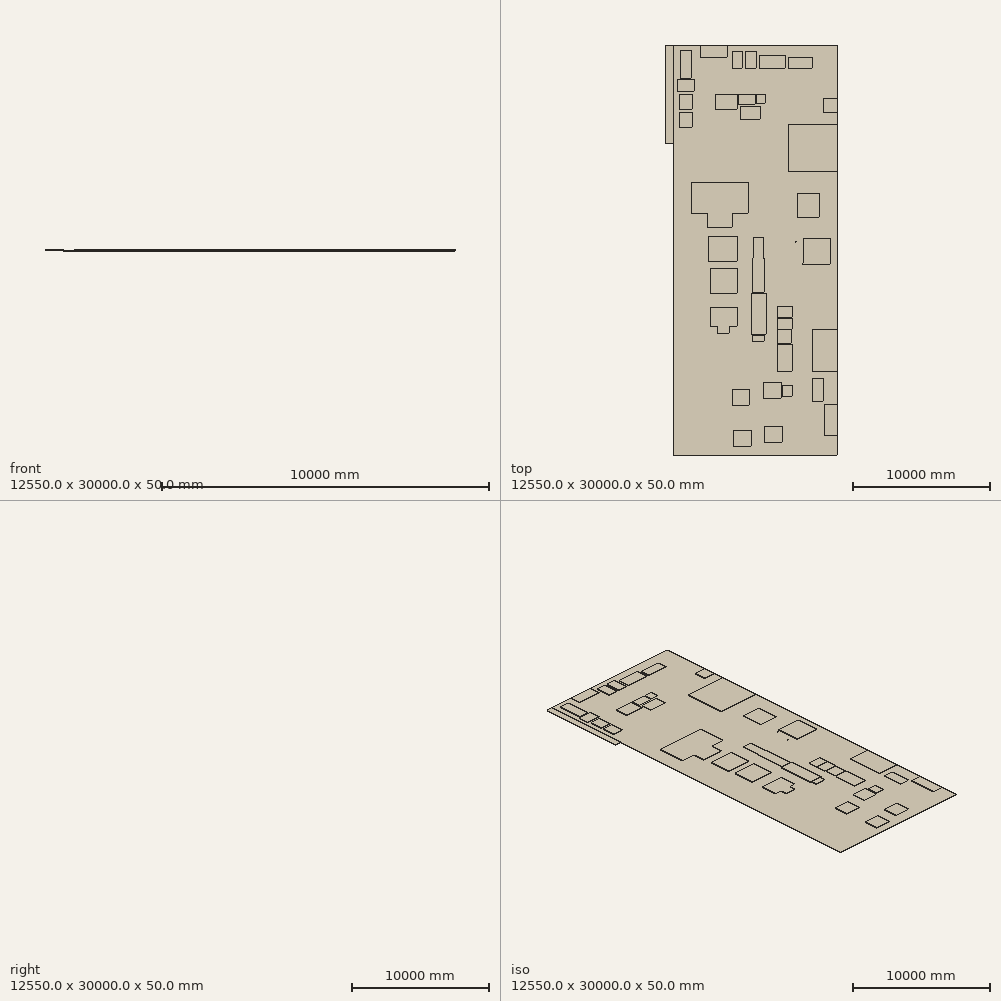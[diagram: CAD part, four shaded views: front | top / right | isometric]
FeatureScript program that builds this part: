
annotation { "Feature Type Name" : "Feature", "Feature Type Description" : "" }
export const myFeature = defineFeature(function(context is Context, id is Id, definition is map)
    precondition{}
    {
        {
            var Q0;
            Q0=qCreatedBy(makeId("Top.planeOp"),FACE);
            var sketch = newSketch(context, id + "F0", { "sketchPlane" : qUnion([Q0])});
            skLineSegment(sketch, "E0.bottom", {"start": v(6000, -15000) * mm, "end": v(-6000, -15000) * mm});
            skLineSegment(sketch, "E0.top", {"start": v(6000, 15000) * mm, "end": v(-6000, 15000) * mm});
            skLineSegment(sketch, "E0.left", {"start": v(6000, -15000) * mm, "end": v(6000, 15000) * mm});
            skLineSegment(sketch, "E0.right", {"start": v(-6000, -15000) * mm, "end": v(-6000, 15000) * mm});
            skPoint(sketch, "E0.middle", {"position": v(0, 0) * mm});
            skSolve(sketch);
        }
        {
            var Q0;
            Q0 = qSketchRegion(id + "F0", true);
            extrude(context, id + "F1", {"entities" : qUnion([Q0]), "depth" : 25 * mm, "offsetDistance" : 25 * mm});
        }
        {
            var Q0;
            Q0=makeQuery(id+"F1.opExtrude","CAP_FACE",FACE,{"disambiguationData":[OSD([sQuery(id+"F0.wireOp",EDGE,"E0.bottom"),sQuery(id+"F0.wireOp",EDGE,"E0.top"),sQuery(id+"F0.wireOp",EDGE,"E0.left"),sQuery(id+"F0.wireOp",EDGE,"E0.right")])],"isStart":false});
            var sketch = newSketch(context, id + "F2", { "sketchPlane" : qUnion([Q0])});
            skLineSegment(sketch, "E1.bottom", {"start": v(-4000, 15000) * mm, "end": v(-2000, 15000) * mm});
            skLineSegment(sketch, "E1.top", {"start": v(-4000, 14100) * mm, "end": v(-2000, 14100) * mm});
            skLineSegment(sketch, "E1.left", {"start": v(-4000, 15000) * mm, "end": v(-4000, 14100) * mm});
            skLineSegment(sketch, "E1.right", {"start": v(-2000, 15000) * mm, "end": v(-2000, 14100) * mm});
            skLineSegment(sketch, "E2.bottom", {"start": v(-1700, 14550) * mm, "end": v(-900, 14550) * mm});
            skLineSegment(sketch, "E2.top", {"start": v(-1700, 13300) * mm, "end": v(-900, 13300) * mm});
            skLineSegment(sketch, "E2.left", {"start": v(-1700, 14550) * mm, "end": v(-1700, 13300) * mm});
            skLineSegment(sketch, "E2.right", {"start": v(-900, 14550) * mm, "end": v(-900, 13300) * mm});
            skLineSegment(sketch, "E3.bottom", {"start": v(-700, 14550) * mm, "end": v(100, 14550) * mm});
            skLineSegment(sketch, "E3.top", {"start": v(-700, 13300) * mm, "end": v(100, 13300) * mm});
            skLineSegment(sketch, "E3.left", {"start": v(-700, 14550) * mm, "end": v(-700, 13300) * mm});
            skLineSegment(sketch, "E3.right", {"start": v(100, 14550) * mm, "end": v(100, 13300) * mm});
            skSolve(sketch);
        }
        {
            var Q0;
            Q0 = qSketchRegion(id + "F2", true);
            extrude(context, id + "F3", {"entities" : qUnion([Q0]), "depth" : 25 * mm, "offsetDistance" : 25 * mm});
        }
        {
            var Q0;
            Q0=makeQuery(id+"F1.opExtrude","CAP_FACE",FACE,{"disambiguationData":[OSD([sQuery(id+"F0.wireOp",EDGE,"E0.bottom"),sQuery(id+"F0.wireOp",EDGE,"E0.top"),sQuery(id+"F0.wireOp",EDGE,"E0.left"),sQuery(id+"F0.wireOp",EDGE,"E0.right")])],"isStart":false});
            var sketch = newSketch(context, id + "F4", { "sketchPlane" : qUnion([Q0])});
            skLineSegment(sketch, "E4.bottom", {"start": v(300, 14300) * mm, "end": v(2200, 14300) * mm});
            skLineSegment(sketch, "E4.top", {"start": v(300, 13300) * mm, "end": v(2200, 13300) * mm});
            skLineSegment(sketch, "E4.left", {"start": v(300, 14300) * mm, "end": v(300, 13300) * mm});
            skLineSegment(sketch, "E4.right", {"start": v(2200, 14300) * mm, "end": v(2200, 13300) * mm});
            skLineSegment(sketch, "E5.bottom", {"start": v(2400, 13300) * mm, "end": v(4200, 13300) * mm});
            skLineSegment(sketch, "E5.top", {"start": v(2400, 14100) * mm, "end": v(4200, 14100) * mm});
            skLineSegment(sketch, "E5.left", {"start": v(2400, 13300) * mm, "end": v(2400, 14100) * mm});
            skLineSegment(sketch, "E5.right", {"start": v(4200, 13300) * mm, "end": v(4200, 14100) * mm});
            skSolve(sketch);
        }
        {
            var Q0;
            Q0 = qSketchRegion(id + "F4", true);
            extrude(context, id + "F5", {"entities" : qUnion([Q0]), "depth" : 25 * mm, "offsetDistance" : 25 * mm});
        }
        {
            var Q0;
            Q0=makeQuery(id+"F1.opExtrude","CAP_FACE",FACE,{"disambiguationData":[OSD([sQuery(id+"F0.wireOp",EDGE,"E0.bottom"),sQuery(id+"F0.wireOp",EDGE,"E0.top"),sQuery(id+"F0.wireOp",EDGE,"E0.left"),sQuery(id+"F0.wireOp",EDGE,"E0.right")])],"isStart":false});
            var sketch = newSketch(context, id + "F6", { "sketchPlane" : qUnion([Q0])});
            skLineSegment(sketch, "E6.bottom", {"start": v(6000, 11100) * mm, "end": v(5000, 11100) * mm});
            skLineSegment(sketch, "E6.top", {"start": v(6000, 10100) * mm, "end": v(5000, 10100) * mm});
            skLineSegment(sketch, "E6.left", {"start": v(6000, 11100) * mm, "end": v(6000, 10100) * mm});
            skLineSegment(sketch, "E6.right", {"start": v(5000, 11100) * mm, "end": v(5000, 10100) * mm});
            skSolve(sketch);
        }
        {
            var Q0;
            Q0 = qSketchRegion(id + "F6", true);
            extrude(context, id + "F7", {"entities" : qUnion([Q0]), "depth" : 25 * mm, "offsetDistance" : 25 * mm});
        }
        {
            var Q0;
            Q0=makeQuery(id+"F1.opExtrude","CAP_FACE",FACE,{"disambiguationData":[OSD([sQuery(id+"F0.wireOp",EDGE,"E0.bottom"),sQuery(id+"F0.wireOp",EDGE,"E0.top"),sQuery(id+"F0.wireOp",EDGE,"E0.left"),sQuery(id+"F0.wireOp",EDGE,"E0.right")])],"isStart":false});
            var sketch = newSketch(context, id + "F8", { "sketchPlane" : qUnion([Q0])});
            skLineSegment(sketch, "E7.bottom", {"start": v(-2900, 11400) * mm, "end": v(-1300, 11400) * mm});
            skLineSegment(sketch, "E7.top", {"start": v(-2900, 10300) * mm, "end": v(-1300, 10300) * mm});
            skLineSegment(sketch, "E7.left", {"start": v(-2900, 11400) * mm, "end": v(-2900, 10300) * mm});
            skLineSegment(sketch, "E7.right", {"start": v(-1300, 11400) * mm, "end": v(-1300, 10300) * mm});
            skLineSegment(sketch, "E8.bottom", {"start": v(-1200, 11400) * mm, "end": v(0, 11400) * mm});
            skLineSegment(sketch, "E8.top", {"start": v(-1200, 10700) * mm, "end": v(0, 10700) * mm});
            skLineSegment(sketch, "E8.left", {"start": v(-1200, 11400) * mm, "end": v(-1200, 10700) * mm});
            skLineSegment(sketch, "E8.right", {"start": v(0, 11400) * mm, "end": v(0, 10700) * mm});
            skLineSegment(sketch, "E9.bottom", {"start": v(100, 11400) * mm, "end": v(750, 11400) * mm});
            skLineSegment(sketch, "E9.top", {"start": v(100, 10750) * mm, "end": v(750, 10750) * mm});
            skLineSegment(sketch, "E9.left", {"start": v(100, 11400) * mm, "end": v(100, 10750) * mm});
            skLineSegment(sketch, "E9.right", {"start": v(750, 11400) * mm, "end": v(750, 10750) * mm});
            skSolve(sketch);
        }
        {
            var Q0;
            Q0 = qSketchRegion(id + "F8", true);
            extrude(context, id + "F9", {"entities" : qUnion([Q0]), "depth" : 25 * mm, "offsetDistance" : 25 * mm});
        }
        {
            var Q0;
            Q0=makeQuery(id+"F1.opExtrude","CAP_FACE",FACE,{"disambiguationData":[OSD([sQuery(id+"F0.wireOp",EDGE,"E0.bottom"),sQuery(id+"F0.wireOp",EDGE,"E0.top"),sQuery(id+"F0.wireOp",EDGE,"E0.left"),sQuery(id+"F0.wireOp",EDGE,"E0.right")])],"isStart":false});
            var sketch = newSketch(context, id + "F10", { "sketchPlane" : qUnion([Q0])});
            skLineSegment(sketch, "E10.bottom", {"start": v(-1100, 10500) * mm, "end": v(400, 10500) * mm});
            skLineSegment(sketch, "E10.top", {"start": v(-1100, 9600) * mm, "end": v(400, 9600) * mm});
            skLineSegment(sketch, "E10.left", {"start": v(-1100, 10500) * mm, "end": v(-1100, 9600) * mm});
            skLineSegment(sketch, "E10.right", {"start": v(400, 10500) * mm, "end": v(400, 9600) * mm});
            skSolve(sketch);
        }
        {
            var Q0;
            Q0 = qSketchRegion(id + "F10", true);
            extrude(context, id + "F11", {"entities" : qUnion([Q0]), "depth" : 25 * mm, "offsetDistance" : 25 * mm});
        }
        {
            var Q0;
            Q0=makeQuery(id+"F1.opExtrude","CAP_FACE",FACE,{"disambiguationData":[OSD([sQuery(id+"F0.wireOp",EDGE,"E0.bottom"),sQuery(id+"F0.wireOp",EDGE,"E0.top"),sQuery(id+"F0.wireOp",EDGE,"E0.left"),sQuery(id+"F0.wireOp",EDGE,"E0.right")])],"isStart":false});
            var sketch = newSketch(context, id + "F12", { "sketchPlane" : qUnion([Q0])});
            skLineSegment(sketch, "E11.bottom", {"start": v(-5500, 14600) * mm, "end": v(-4650, 14600) * mm});
            skLineSegment(sketch, "E11.top", {"start": v(-5500, 12600) * mm, "end": v(-4650, 12600) * mm});
            skLineSegment(sketch, "E11.left", {"start": v(-5500, 14600) * mm, "end": v(-5500, 12600) * mm});
            skLineSegment(sketch, "E11.right", {"start": v(-4650, 14600) * mm, "end": v(-4650, 12600) * mm});
            skLineSegment(sketch, "E12.bottom", {"start": v(-5675, 12500) * mm, "end": v(-4475, 12500) * mm});
            skLineSegment(sketch, "E12.top", {"start": v(-5675, 11600) * mm, "end": v(-4475, 11600) * mm});
            skLineSegment(sketch, "E12.left", {"start": v(-5675, 12500) * mm, "end": v(-5675, 11600) * mm});
            skLineSegment(sketch, "E12.right", {"start": v(-4475, 12500) * mm, "end": v(-4475, 11600) * mm});
            skLineSegment(sketch, "E13.bottom", {"start": v(-5525, 11400) * mm, "end": v(-4625, 11400) * mm});
            skLineSegment(sketch, "E13.top", {"start": v(-5525, 10300) * mm, "end": v(-4625, 10300) * mm});
            skLineSegment(sketch, "E13.left", {"start": v(-5525, 11400) * mm, "end": v(-5525, 10300) * mm});
            skLineSegment(sketch, "E13.right", {"start": v(-4625, 11400) * mm, "end": v(-4625, 10300) * mm});
            skLineSegment(sketch, "E14.bottom", {"start": v(-5525, 10100) * mm, "end": v(-4625, 10100) * mm});
            skLineSegment(sketch, "E14.top", {"start": v(-5525, 9000) * mm, "end": v(-4625, 9000) * mm});
            skLineSegment(sketch, "E14.left", {"start": v(-5525, 10100) * mm, "end": v(-5525, 9000) * mm});
            skLineSegment(sketch, "E14.right", {"start": v(-4625, 10100) * mm, "end": v(-4625, 9000) * mm});
            skSolve(sketch);
        }
        {
            var Q0;
            Q0 = qSketchRegion(id + "F12", true);
            extrude(context, id + "F13", {"entities" : qUnion([Q0]), "depth" : 25 * mm, "offsetDistance" : 25 * mm});
        }
        {
            var Q0;
            Q0=makeQuery(id+"F1.opExtrude","CAP_FACE",FACE,{"disambiguationData":[OSD([sQuery(id+"F0.wireOp",EDGE,"E0.bottom"),sQuery(id+"F0.wireOp",EDGE,"E0.top"),sQuery(id+"F0.wireOp",EDGE,"E0.left"),sQuery(id+"F0.wireOp",EDGE,"E0.right")])],"isStart":false});
            var sketch = newSketch(context, id + "F14", { "sketchPlane" : qUnion([Q0])});
            skLineSegment(sketch, "E15.bottom", {"start": v(-6000, 15000) * mm, "end": v(-6550, 15000) * mm});
            skLineSegment(sketch, "E15.top", {"start": v(-6000, 7800) * mm, "end": v(-6550, 7800) * mm});
            skLineSegment(sketch, "E15.left", {"start": v(-6000, 15000) * mm, "end": v(-6000, 7800) * mm});
            skLineSegment(sketch, "E15.right", {"start": v(-6550, 15000) * mm, "end": v(-6550, 7800) * mm});
            skSolve(sketch);
        }
        {
            var Q0;
            Q0 = qSketchRegion(id + "F14", true);
            extrude(context, id + "F15", {"entities" : qUnion([Q0]), "depth" : 25 * mm, "offsetDistance" : 25 * mm});
        }
        {
            var Q0;
            Q0=makeQuery(id+"F1.opExtrude","CAP_FACE",FACE,{"disambiguationData":[OSD([sQuery(id+"F0.wireOp",EDGE,"E0.bottom"),sQuery(id+"F0.wireOp",EDGE,"E0.top"),sQuery(id+"F0.wireOp",EDGE,"E0.left"),sQuery(id+"F0.wireOp",EDGE,"E0.right")])],"isStart":false});
            var sketch = newSketch(context, id + "F16", { "sketchPlane" : qUnion([Q0])});
            skLineSegment(sketch, "E16.bottom", {"start": v(6000, 9200) * mm, "end": v(2400, 9200) * mm});
            skLineSegment(sketch, "E16.top", {"start": v(6000, 5800) * mm, "end": v(2400, 5800) * mm});
            skLineSegment(sketch, "E16.left", {"start": v(6000, 9200) * mm, "end": v(6000, 5800) * mm});
            skLineSegment(sketch, "E16.right", {"start": v(2400, 9200) * mm, "end": v(2400, 5800) * mm});
            skLineSegment(sketch, "E17.bottom", {"start": v(3100, 4200) * mm, "end": v(4700, 4200) * mm});
            skLineSegment(sketch, "E17.top", {"start": v(3100, 2400) * mm, "end": v(4700, 2400) * mm});
            skLineSegment(sketch, "E17.left", {"start": v(3100, 4200) * mm, "end": v(3100, 2400) * mm});
            skLineSegment(sketch, "E17.right", {"start": v(4700, 4200) * mm, "end": v(4700, 2400) * mm});
            skSolve(sketch);
        }
        {
            var Q0;
            Q0 = qSketchRegion(id + "F16", true);
            extrude(context, id + "F17", {"entities" : qUnion([Q0]), "depth" : 25 * mm, "offsetDistance" : 25 * mm});
        }
        {
            var Q0;
            Q0=makeQuery(id+"F1.opExtrude","CAP_FACE",FACE,{"disambiguationData":[OSD([sQuery(id+"F0.wireOp",EDGE,"E0.bottom"),sQuery(id+"F0.wireOp",EDGE,"E0.top"),sQuery(id+"F0.wireOp",EDGE,"E0.left"),sQuery(id+"F0.wireOp",EDGE,"E0.right")])],"isStart":false});
            var sketch = newSketch(context, id + "F18", { "sketchPlane" : qUnion([Q0])});
            skLineSegment(sketch, "E18.bottom", {"start": v(5500, 900) * mm, "end": v(3500, 900) * mm});
            skLineSegment(sketch, "E18.top", {"start": v(5500, -1000) * mm, "end": v(3500, -1000) * mm});
            skLineSegment(sketch, "E18.left", {"start": v(5500, 900) * mm, "end": v(5500, -1000) * mm});
            skLineSegment(sketch, "E18.right", {"start": v(3500, 910) * mm, "end": v(3500, -990) * mm});
            skLineSegment(sketch, "E19", {"start": v(2933.85, 593.98) * mm, "end": v(3500, 900) * mm});
            skLineSegment(sketch, "E20", {"start": v(3500, -1000) * mm, "end": v(2925.99, -581.08) * mm});
            skLineSegment(sketch, "E21", {"start": v(2925.99, -581.08) * mm, "end": v(2930.75, -574.56) * mm});
            skLineSegment(sketch, "E22", {"start": v(2930.75, -574.56) * mm, "end": v(3500, -990) * mm});
            skLineSegment(sketch, "E23", {"start": v(2927.84, 605.1) * mm, "end": v(2933.85, 593.98) * mm});
            skLineSegment(sketch, "E24", {"start": v(2927.84, 605.1) * mm, "end": v(3500, 910) * mm});
            skSolve(sketch);
        }
        {
            var Q0;
            Q0 = qSketchRegion(id + "F18", true);
            extrude(context, id + "F19", {"entities" : qUnion([Q0]), "depth" : 25 * mm, "offsetDistance" : 25 * mm});
        }
        {
            var Q0;
            Q0=makeQuery(id+"F1.opExtrude","CAP_FACE",FACE,{"disambiguationData":[OSD([sQuery(id+"F0.wireOp",EDGE,"E0.bottom"),sQuery(id+"F0.wireOp",EDGE,"E0.top"),sQuery(id+"F0.wireOp",EDGE,"E0.left"),sQuery(id+"F0.wireOp",EDGE,"E0.right")])],"isStart":false});
            var sketch = newSketch(context, id + "F20", { "sketchPlane" : qUnion([Q0])});
            skLineSegment(sketch, "E25.bottom", {"start": v(1900, -9650) * mm, "end": v(600, -9650) * mm});
            skLineSegment(sketch, "E25.top", {"start": v(1900, -10850) * mm, "end": v(600, -10850) * mm});
            skLineSegment(sketch, "E25.left", {"start": v(1900, -9650) * mm, "end": v(1900, -10850) * mm});
            skLineSegment(sketch, "E25.right", {"start": v(600, -9650) * mm, "end": v(600, -10850) * mm});
            skLineSegment(sketch, "E26.bottom", {"start": v(-1700, -10150) * mm, "end": v(-400, -10150) * mm});
            skLineSegment(sketch, "E26.top", {"start": v(-1700, -11350) * mm, "end": v(-400, -11350) * mm});
            skLineSegment(sketch, "E26.left", {"start": v(-1700, -10150) * mm, "end": v(-1700, -11350) * mm});
            skLineSegment(sketch, "E26.right", {"start": v(-400, -10150) * mm, "end": v(-400, -11350) * mm});
            skLineSegment(sketch, "E27.bottom", {"start": v(700, -12850) * mm, "end": v(2000, -12850) * mm});
            skLineSegment(sketch, "E27.top", {"start": v(700, -14050) * mm, "end": v(2000, -14050) * mm});
            skLineSegment(sketch, "E27.left", {"start": v(700, -12850) * mm, "end": v(700, -14050) * mm});
            skLineSegment(sketch, "E27.right", {"start": v(2000, -12850) * mm, "end": v(2000, -14050) * mm});
            skLineSegment(sketch, "E28.bottom", {"start": v(-1600, -13150) * mm, "end": v(-300, -13150) * mm});
            skLineSegment(sketch, "E28.top", {"start": v(-1600, -14350) * mm, "end": v(-300, -14350) * mm});
            skLineSegment(sketch, "E28.left", {"start": v(-1600, -13150) * mm, "end": v(-1600, -14350) * mm});
            skLineSegment(sketch, "E28.right", {"start": v(-300, -13150) * mm, "end": v(-300, -14350) * mm});
            skSolve(sketch);
        }
        {
            var Q0;
            Q0 = qSketchRegion(id + "F20", true);
            extrude(context, id + "F21", {"entities" : qUnion([Q0]), "depth" : 25 * mm, "offsetDistance" : 25 * mm});
        }
        {
            var Q0;
            Q0=makeQuery(id+"F1.opExtrude","CAP_FACE",FACE,{"disambiguationData":[OSD([sQuery(id+"F0.wireOp",EDGE,"E0.bottom"),sQuery(id+"F0.wireOp",EDGE,"E0.top"),sQuery(id+"F0.wireOp",EDGE,"E0.left"),sQuery(id+"F0.wireOp",EDGE,"E0.right")])],"isStart":false});
            var sketch = newSketch(context, id + "F22", { "sketchPlane" : qUnion([Q0])});
            skLineSegment(sketch, "E29.bottom", {"start": v(-4700, 5000) * mm, "end": v(-500, 5000) * mm});
            skLineSegment(sketch, "E29.top", {"start": v(-4700, 2700) * mm, "end": v(-3500, 2700) * mm});
            skLineSegment(sketch, "E29.left", {"start": v(-4700, 5000) * mm, "end": v(-4700, 2700) * mm});
            skLineSegment(sketch, "E29.right", {"start": v(-500, 5000) * mm, "end": v(-500, 2700) * mm});
            skLineSegment(sketch, "E30.top", {"start": v(-3500, 1700) * mm, "end": v(-1700, 1700) * mm});
            skLineSegment(sketch, "E30.left", {"start": v(-3500, 2700) * mm, "end": v(-3500, 1700) * mm});
            skLineSegment(sketch, "E30.right", {"start": v(-1700, 2700) * mm, "end": v(-1700, 1700) * mm});
            skLineSegment(sketch, "E31.trimOffspring", {"start": v(-1700, 2700) * mm, "end": v(-500, 2700) * mm});
            skLineSegment(sketch, "E32.bottom", {"start": v(-3400, 1000) * mm, "end": v(-1300, 1000) * mm});
            skLineSegment(sketch, "E32.top", {"start": v(-3400, -800) * mm, "end": v(-1300, -800) * mm});
            skLineSegment(sketch, "E32.left", {"start": v(-3400, 1000) * mm, "end": v(-3400, -800) * mm});
            skLineSegment(sketch, "E32.right", {"start": v(-1300, 1000) * mm, "end": v(-1300, -800) * mm});
            skLineSegment(sketch, "E33.bottom", {"start": v(-3300, -1300) * mm, "end": v(-1300, -1300) * mm});
            skLineSegment(sketch, "E33.top", {"start": v(-3300, -3150) * mm, "end": v(-1300, -3150) * mm});
            skLineSegment(sketch, "E33.left", {"start": v(-3300, -1300) * mm, "end": v(-3300, -3150) * mm});
            skLineSegment(sketch, "E33.right", {"start": v(-1300, -1300) * mm, "end": v(-1300, -3150) * mm});
            skLineSegment(sketch, "E34.bottom", {"start": v(-3300, -4150) * mm, "end": v(-1300, -4150) * mm});
            skLineSegment(sketch, "E34.top", {"start": v(-3300, -5550) * mm, "end": v(-2750, -5550) * mm});
            skLineSegment(sketch, "E34.left", {"start": v(-3300, -4150) * mm, "end": v(-3300, -5550) * mm});
            skLineSegment(sketch, "E34.right", {"start": v(-1300, -4150) * mm, "end": v(-1300, -5550) * mm});
            skLineSegment(sketch, "E35.top", {"start": v(-2750, -6100) * mm, "end": v(-1850, -6100) * mm});
            skLineSegment(sketch, "E35.left", {"start": v(-2750, -5550) * mm, "end": v(-2750, -6100) * mm});
            skLineSegment(sketch, "E35.right", {"start": v(-1850, -5550) * mm, "end": v(-1850, -6100) * mm});
            skLineSegment(sketch, "E36.trimOffspring", {"start": v(-1850, -5550) * mm, "end": v(-1300, -5550) * mm});
            skSolve(sketch);
        }
        {
            var Q0;
            Q0 = qSketchRegion(id + "F22", true);
            extrude(context, id + "F23", {"entities" : qUnion([Q0]), "depth" : 25 * mm, "offsetDistance" : 25 * mm});
        }
        {
            var Q0;
            Q0=makeQuery(id+"F1.opExtrude","CAP_FACE",FACE,{"disambiguationData":[OSD([sQuery(id+"F0.wireOp",EDGE,"E0.bottom"),sQuery(id+"F0.wireOp",EDGE,"E0.top"),sQuery(id+"F0.wireOp",EDGE,"E0.left"),sQuery(id+"F0.wireOp",EDGE,"E0.right")])],"isStart":false});
            var sketch = newSketch(context, id + "F24", { "sketchPlane" : qUnion([Q0])});
            skLineSegment(sketch, "E37.bottom", {"start": v(5100, -11250) * mm, "end": v(6000, -11250) * mm});
            skLineSegment(sketch, "E37.top", {"start": v(5100, -13550) * mm, "end": v(6000, -13550) * mm});
            skLineSegment(sketch, "E37.left", {"start": v(5100, -11250) * mm, "end": v(5100, -13550) * mm});
            skLineSegment(sketch, "E37.right", {"start": v(6000, -11250) * mm, "end": v(6000, -13550) * mm});
            skSolve(sketch);
        }
        {
            var Q0;
            Q0 = qSketchRegion(id + "F24", true);
            extrude(context, id + "F25", {"entities" : qUnion([Q0]), "depth" : 25 * mm, "offsetDistance" : 25 * mm});
        }
        {
            var Q0;
            Q0=makeQuery(id+"F1.opExtrude","CAP_FACE",FACE,{"disambiguationData":[OSD([sQuery(id+"F0.wireOp",EDGE,"E0.bottom"),sQuery(id+"F0.wireOp",EDGE,"E0.top"),sQuery(id+"F0.wireOp",EDGE,"E0.left"),sQuery(id+"F0.wireOp",EDGE,"E0.right")])],"isStart":false});
            var sketch = newSketch(context, id + "F26", { "sketchPlane" : qUnion([Q0])});
            skLineSegment(sketch, "E38.bottom", {"start": v(-200, -6200) * mm, "end": v(700, -6200) * mm});
            skLineSegment(sketch, "E38.top", {"start": v(-200, -6650) * mm, "end": v(700, -6650) * mm});
            skLineSegment(sketch, "E38.left", {"start": v(-200, -6200) * mm, "end": v(-200, -6650) * mm});
            skLineSegment(sketch, "E38.right", {"start": v(700, -6200) * mm, "end": v(700, -6650) * mm});
            skLineSegment(sketch, "E39.bottom", {"start": v(800, -6150) * mm, "end": v(-300, -6150) * mm});
            skLineSegment(sketch, "E39.top", {"start": v(800, -3150) * mm, "end": v(-300, -3150) * mm});
            skLineSegment(sketch, "E39.left", {"start": v(800, -6150) * mm, "end": v(800, -3150) * mm});
            skLineSegment(sketch, "E39.right", {"start": v(-300, -6150) * mm, "end": v(-300, -3150) * mm});
            skLineSegment(sketch, "E40.bottom", {"start": v(675, -3050) * mm, "end": v(-175, -3050) * mm});
            skLineSegment(sketch, "E40.top", {"start": v(675, -550) * mm, "end": v(625, -550) * mm});
            skLineSegment(sketch, "E40.left", {"start": v(675, -3050) * mm, "end": v(675, -550) * mm});
            skLineSegment(sketch, "E40.right", {"start": v(-175, -3050) * mm, "end": v(-175, -550) * mm});
            skLineSegment(sketch, "E41.top", {"start": v(-125, 950) * mm, "end": v(625, 950) * mm});
            skLineSegment(sketch, "E41.left", {"start": v(-125, -550) * mm, "end": v(-125, 950) * mm});
            skLineSegment(sketch, "E41.right", {"start": v(625, -550) * mm, "end": v(625, 950) * mm});
            skLineSegment(sketch, "E42.trimOffspring", {"start": v(-125, -550) * mm, "end": v(-175, -550) * mm});
            skSolve(sketch);
        }
        {
            var Q0;
            Q0 = qSketchRegion(id + "F26", true);
            extrude(context, id + "F27", {"entities" : qUnion([Q0]), "depth" : 25 * mm, "offsetDistance" : 25 * mm});
        }
        {
            var Q0;
            Q0=makeQuery(id+"F1.opExtrude","CAP_FACE",FACE,{"disambiguationData":[OSD([sQuery(id+"F0.wireOp",EDGE,"E0.bottom"),sQuery(id+"F0.wireOp",EDGE,"E0.top"),sQuery(id+"F0.wireOp",EDGE,"E0.left"),sQuery(id+"F0.wireOp",EDGE,"E0.right")])],"isStart":false});
            var sketch = newSketch(context, id + "F28", { "sketchPlane" : qUnion([Q0])});
            skLineSegment(sketch, "E43.bottom", {"start": v(5000, -11050) * mm, "end": v(4200, -11050) * mm});
            skLineSegment(sketch, "E43.top", {"start": v(5000, -9350) * mm, "end": v(4200, -9350) * mm});
            skLineSegment(sketch, "E43.left", {"start": v(5000, -11050) * mm, "end": v(5000, -9350) * mm});
            skLineSegment(sketch, "E43.right", {"start": v(4200, -11050) * mm, "end": v(4200, -9350) * mm});
            skLineSegment(sketch, "E44.bottom", {"start": v(6000, -8850) * mm, "end": v(4200, -8850) * mm});
            skLineSegment(sketch, "E44.top", {"start": v(6000, -5800) * mm, "end": v(4200, -5800) * mm});
            skLineSegment(sketch, "E44.left", {"start": v(6000, -8850) * mm, "end": v(6000, -5800) * mm});
            skLineSegment(sketch, "E44.right", {"start": v(4200, -8850) * mm, "end": v(4200, -5800) * mm});
            skSolve(sketch);
        }
        {
            var Q0;
            Q0 = qSketchRegion(id + "F28", true);
            extrude(context, id + "F29", {"entities" : qUnion([Q0]), "depth" : 25 * mm, "offsetDistance" : 25 * mm});
        }
        {
            var Q0;
            Q0=makeQuery(id+"F1.opExtrude","CAP_FACE",FACE,{"disambiguationData":[OSD([sQuery(id+"F0.wireOp",EDGE,"E0.bottom"),sQuery(id+"F0.wireOp",EDGE,"E0.top"),sQuery(id+"F0.wireOp",EDGE,"E0.left"),sQuery(id+"F0.wireOp",EDGE,"E0.right")])],"isStart":false});
            var sketch = newSketch(context, id + "F30", { "sketchPlane" : qUnion([Q0])});
            skLineSegment(sketch, "E45.bottom", {"start": v(1600, -6850) * mm, "end": v(2700, -6850) * mm});
            skLineSegment(sketch, "E45.top", {"start": v(1600, -8850) * mm, "end": v(2700, -8850) * mm});
            skLineSegment(sketch, "E45.left", {"start": v(1600, -6850) * mm, "end": v(1600, -8850) * mm});
            skLineSegment(sketch, "E45.right", {"start": v(2700, -6850) * mm, "end": v(2700, -8850) * mm});
            skLineSegment(sketch, "E46.bottom", {"start": v(2650, -6800) * mm, "end": v(1650, -6800) * mm});
            skLineSegment(sketch, "E46.top", {"start": v(2650, -5800) * mm, "end": v(1650, -5800) * mm});
            skLineSegment(sketch, "E46.left", {"start": v(2650, -6800) * mm, "end": v(2650, -5800) * mm});
            skLineSegment(sketch, "E46.right", {"start": v(1650, -6800) * mm, "end": v(1650, -5800) * mm});
            skLineSegment(sketch, "E47.bottom", {"start": v(1600, -4950) * mm, "end": v(2700, -4950) * mm});
            skLineSegment(sketch, "E47.top", {"start": v(1600, -5750) * mm, "end": v(2700, -5750) * mm});
            skLineSegment(sketch, "E47.left", {"start": v(1600, -4950) * mm, "end": v(1600, -5750) * mm});
            skLineSegment(sketch, "E47.right", {"start": v(2700, -4950) * mm, "end": v(2700, -5750) * mm});
            skLineSegment(sketch, "E48.bottom", {"start": v(2700, -4900) * mm, "end": v(1600, -4900) * mm});
            skLineSegment(sketch, "E48.top", {"start": v(2700, -4100) * mm, "end": v(1600, -4100) * mm});
            skLineSegment(sketch, "E48.left", {"start": v(2700, -4900) * mm, "end": v(2700, -4100) * mm});
            skLineSegment(sketch, "E48.right", {"start": v(1600, -4900) * mm, "end": v(1600, -4100) * mm});
            skSolve(sketch);
        }
        {
            var Q0;
            Q0 = qSketchRegion(id + "F30", true);
            extrude(context, id + "F31", {"entities" : qUnion([Q0]), "depth" : 25 * mm, "offsetDistance" : 25 * mm});
        }
        {
            var Q0;
            Q0=makeQuery(id+"F1.opExtrude","CAP_FACE",FACE,{"disambiguationData":[OSD([sQuery(id+"F0.wireOp",EDGE,"E0.bottom"),sQuery(id+"F0.wireOp",EDGE,"E0.top"),sQuery(id+"F0.wireOp",EDGE,"E0.left"),sQuery(id+"F0.wireOp",EDGE,"E0.right")])],"isStart":false});
            var sketch = newSketch(context, id + "F32", { "sketchPlane" : qUnion([Q0])});
            skLineSegment(sketch, "E49.bottom", {"start": v(2000, -9850) * mm, "end": v(2700, -9850) * mm});
            skLineSegment(sketch, "E49.top", {"start": v(2000, -10700) * mm, "end": v(2700, -10700) * mm});
            skLineSegment(sketch, "E49.left", {"start": v(2000, -9850) * mm, "end": v(2000, -10700) * mm});
            skLineSegment(sketch, "E49.right", {"start": v(2700, -9850) * mm, "end": v(2700, -10700) * mm});
            skSolve(sketch);
        }
        {
            var Q0;
            Q0 = qSketchRegion(id + "F32", true);
            extrude(context, id + "F33", {"entities" : qUnion([Q0]), "depth" : 25 * mm, "offsetDistance" : 25 * mm});
        }
    });
